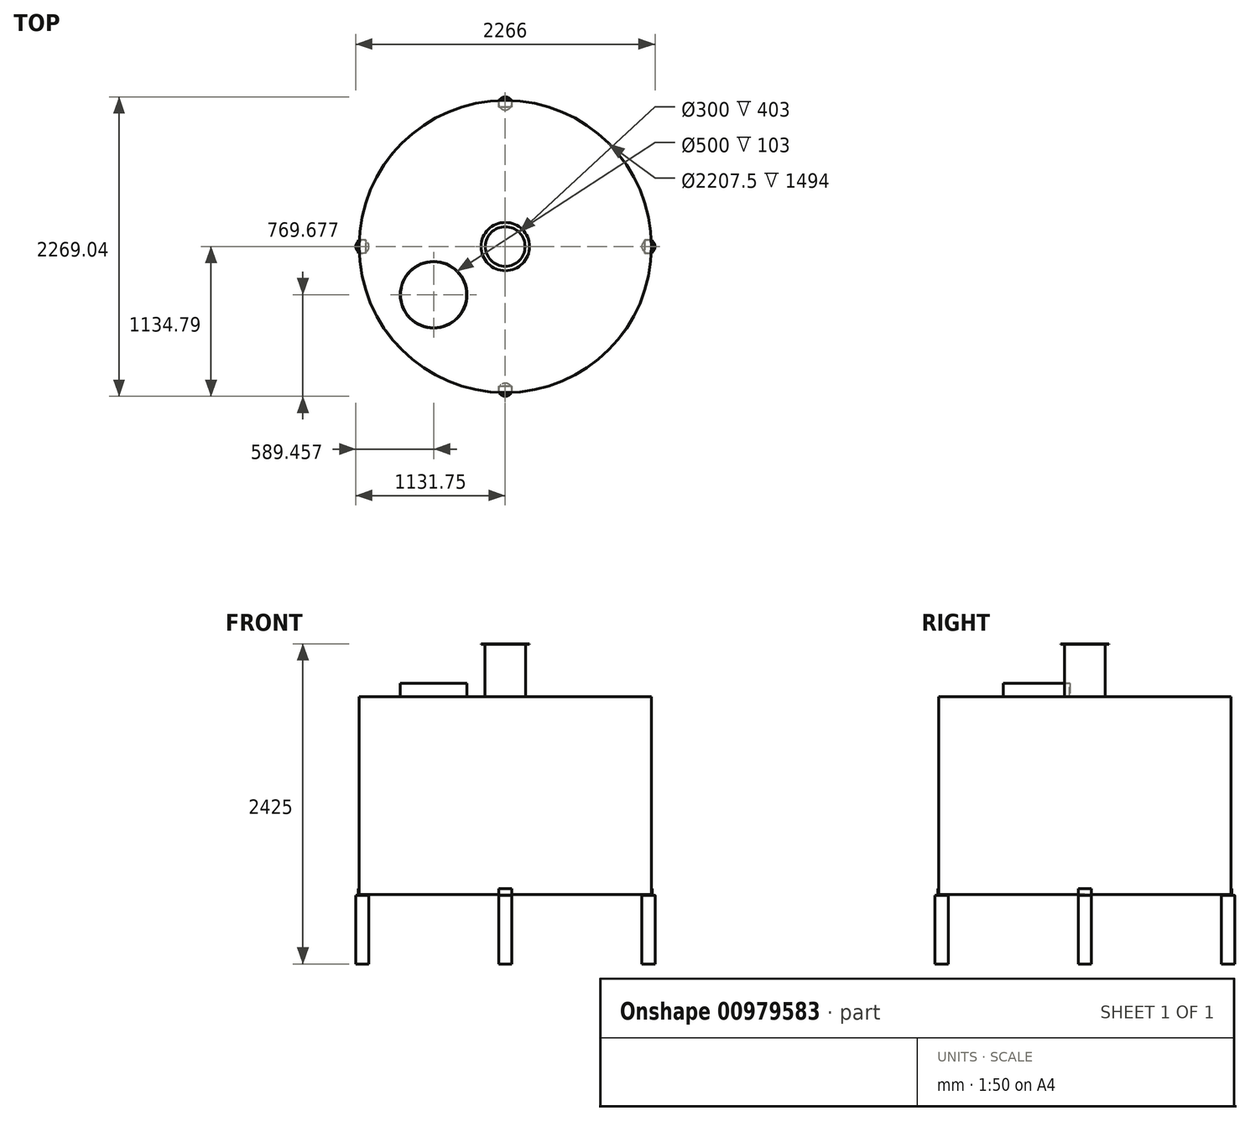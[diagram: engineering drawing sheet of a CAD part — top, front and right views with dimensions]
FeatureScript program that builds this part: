
annotation { "Feature Type Name" : "Feature", "Feature Type Description" : "" }
export const myFeature = defineFeature(function(context is Context, id is Id, definition is map)
    precondition{}
    {
        {
            var Q0;
            Q0=qCreatedBy(makeId("Top.planeOp"),FACE);
            var sketch = newSketch(context, id + "F0", { "sketchPlane" : qUnion([Q0])});
            skCircle(sketch, "E0", {"center": v(0, 0) * mm, "radius": 1106.75 * mm});
            skCircle(sketch, "E1", {"center": v(0, 0) * mm, "radius": 1103.75 * mm});
            skSolve(sketch);
        }
        {
            var Q0;
            Q0=makeQuery(id+"F0.imprint","IMPRINT",FACE,{"disambiguationData":[TD([[makeQuery(id+"F0.imprint","IMPRINT",EDGE,{"derivedFrom":sQuery(id+"F0.wireOp",EDGE,"E0")}),1.0]])]});
            extrude(context, id + "F1", {"entities" : qUnion([Q0]), "oppositeDirection" : true, "depth" : 1500 * mm, "offsetDistance" : 25.4 * mm});
        }
        {
            var Q0;
            Q0=makeQuery(id+"F1.opExtrude","CAP_FACE",FACE,{"disambiguationData":[OSD([sQuery(id+"F0.wireOp",EDGE,"E0"),sQuery(id+"F0.wireOp",EDGE,"E1")])],"isStart":false});
            var sketch = newSketch(context, id + "F2", { "sketchPlane" : qUnion([Q0])});
            skCircle(sketch, "E2", {"center": v(0, 0) * mm, "radius": 1103.75 * mm});
            skSolve(sketch);
        }
        {
            var Q0;
            Q0 = qSketchRegion(id + "F2", true);
            extrude(context, id + "F3", {"entities" : qUnion([Q0]), "operationType" : NewBodyOperationType.ADD, "oppositeDirection" : true, "depth" : 3 * mm, "offsetDistance" : 25.4 * mm});
        }
        {
            var Q0;
            Q0=makeQuery(id+"F1.opExtrude","CAP_FACE",FACE,{"disambiguationData":[OSD([sQuery(id+"F0.wireOp",EDGE,"E0"),sQuery(id+"F0.wireOp",EDGE,"E1")])],"isStart":true});
            var sketch = newSketch(context, id + "F4", { "sketchPlane" : qUnion([Q0])});
            skCircle(sketch, "E3", {"center": v(0, 0) * mm, "radius": 1103.75 * mm});
            skCircle(sketch, "E4", {"center": v(-542.3, -365.11) * mm, "radius": 250 * mm});
            skCircle(sketch, "E5", {"center": v(0, 0) * mm, "radius": 150 * mm});
            skSolve(sketch);
        }
        {
            var Q0;
            Q0 = qSketchRegion(id + "F4", true);
            extrude(context, id + "F5", {"entities" : qUnion([Q0]), "operationType" : NewBodyOperationType.ADD, "oppositeDirection" : true, "depth" : 3 * mm, "offsetDistance" : 25.4 * mm});
        }
        {
            var Q0;
            Q0=makeQuery(id+"F5.boolean.opBoolean","MERGE",FACE,{"derivedFrom":[makeQuery(id+"F1.opExtrude","CAP_FACE",FACE,{"disambiguationData":[OSD([sQuery(id+"F0.wireOp",EDGE,"E0"),sQuery(id+"F0.wireOp",EDGE,"E1")])],"isStart":true}),makeQuery(id+"F5.opExtrude","CAP_FACE",FACE,{"disambiguationData":[OSD([sQuery(id+"F4.wireOp",EDGE,"E3"),sQuery(id+"F4.wireOp",EDGE,"E4"),sQuery(id+"F4.wireOp",EDGE,"E5")])],"isStart":true})]});
            var sketch = newSketch(context, id + "F6", { "sketchPlane" : qUnion([Q0])});
            skCircle(sketch, "E6", {"center": v(-542.3, -365.11) * mm, "radius": 253 * mm});
            skCircle(sketch, "E7", {"center": v(-542.3, -365.11) * mm, "radius": 250 * mm});
            skSolve(sketch);
        }
        {
            var Q0;
            Q0 = qSketchRegion(id + "F6", true);
            extrude(context, id + "F7", {"entities" : qUnion([Q0]), "operationType" : NewBodyOperationType.ADD, "depth" : 100 * mm, "offsetDistance" : 25.4 * mm});
        }
        {
            var Q0;
            Q0=makeQuery(id+"F5.boolean.opBoolean","MERGE",FACE,{"derivedFrom":[makeQuery(id+"F1.opExtrude","CAP_FACE",FACE,{"disambiguationData":[OSD([sQuery(id+"F0.wireOp",EDGE,"E0"),sQuery(id+"F0.wireOp",EDGE,"E1")])],"isStart":true}),makeQuery(id+"F5.opExtrude","CAP_FACE",FACE,{"disambiguationData":[OSD([sQuery(id+"F4.wireOp",EDGE,"E3"),sQuery(id+"F4.wireOp",EDGE,"E4"),sQuery(id+"F4.wireOp",EDGE,"E5")])],"isStart":true})]});
            var sketch = newSketch(context, id + "F8", { "sketchPlane" : qUnion([Q0])});
            skCircle(sketch, "E8", {"center": v(0, 0) * mm, "radius": 153 * mm});
            skCircle(sketch, "E9", {"center": v(0, 0) * mm, "radius": 150 * mm});
            skSolve(sketch);
        }
        {
            var Q0;
            Q0 = qSketchRegion(id + "F8", true);
            extrude(context, id + "F9", {"entities" : qUnion([Q0]), "operationType" : NewBodyOperationType.ADD, "depth" : 400 * mm, "offsetDistance" : 25.4 * mm});
        }
        {
            var Q0;
            Q0=makeQuery(id+"F9.opExtrude","CAP_FACE",FACE,{"disambiguationData":[OSD([sQuery(id+"F8.wireOp",EDGE,"E8"),sQuery(id+"F8.wireOp",EDGE,"E9")])],"isStart":false});
            var sketch = newSketch(context, id + "F10", { "sketchPlane" : qUnion([Q0])});
            skCircle(sketch, "E10", {"center": v(0, 0) * mm, "radius": 183 * mm});
            skCircle(sketch, "E11", {"center": v(0, 0) * mm, "radius": 150 * mm});
            skSolve(sketch);
        }
        {
            var Q0;
            Q0 = qSketchRegion(id + "F10", true);
            extrude(context, id + "F11", {"entities" : qUnion([Q0]), "operationType" : NewBodyOperationType.ADD, "oppositeDirection" : true, "depth" : 3 * mm, "offsetDistance" : 25.4 * mm});
        }
        {
            var Q0;
            Q0=qCreatedBy(makeId("Front.planeOp"),FACE);
            cPlane(context, id + "F12", {"entities" : qUnion([Q0]), "cplaneType" : CPlaneType.OFFSET, "offset" : 1107.3 * mm, "width" : 152.4 * mm, "height" : 152.4 * mm});
        }
        {
            var Q0;
            Q0=qCreatedBy(id+"F12.planeOp",FACE);
            var sketch = newSketch(context, id + "F13", { "sketchPlane" : qUnion([Q0])});
            skLineSegment(sketch, "E12.bottom", {"start": v(-50, -1455) * mm, "end": v(50, -1455) * mm});
            skLineSegment(sketch, "E12.top", {"start": v(-50, -1505) * mm, "end": v(50, -1505) * mm});
            skLineSegment(sketch, "E12.left", {"start": v(-50, -1455) * mm, "end": v(-50, -1505) * mm});
            skLineSegment(sketch, "E12.right", {"start": v(50, -1455) * mm, "end": v(50, -1505) * mm});
            skLineSegment(sketch, "E13", {"start": v(0, -595.76) * mm, "end": v(0, -412.86) * mm, "construction": true});
            skSolve(sketch);
        }
        {
            var Q0;
            Q0 = qSketchRegion(id + "F13", true);
            extrude(context, id + "F14", {"entities" : qUnion([Q0]), "depth" : 5 * mm, "offsetDistance" : 25.4 * mm});
        }
        {
            var Q0;
            Q0=makeQuery(id+"F14.opExtrude","CAP_FACE",FACE,{"disambiguationData":[OSD([sQuery(id+"F13.wireOp",EDGE,"E12.bottom"),sQuery(id+"F13.wireOp",EDGE,"E12.top"),sQuery(id+"F13.wireOp",EDGE,"E12.left"),sQuery(id+"F13.wireOp",EDGE,"E12.right")])],"isStart":true});
            var sketch = newSketch(context, id + "F15", { "sketchPlane" : qUnion([Q0])});
            skLineSegment(sketch, "E14.bottom", {"start": v(-50, -1505) * mm, "end": v(50, -1505) * mm});
            skLineSegment(sketch, "E14.top", {"start": v(-50, -1500) * mm, "end": v(50, -1500) * mm});
            skLineSegment(sketch, "E14.left", {"start": v(-50, -1505) * mm, "end": v(-50, -1500) * mm});
            skLineSegment(sketch, "E14.right", {"start": v(50, -1505) * mm, "end": v(50, -1500) * mm});
            skSolve(sketch);
        }
        {
            var Q0;
            Q0 = qSketchRegion(id + "F15", true);
            extrude(context, id + "F16", {"entities" : qUnion([Q0]), "operationType" : NewBodyOperationType.ADD, "depth" : 50 * mm, "offsetDistance" : 25.4 * mm});
        }
        {
            var Q0;
            Q0=qCreatedBy(id+"F12.planeOp",FACE);
            cPlane(context, id + "F17", {"entities" : qUnion([Q0]), "cplaneType" : CPlaneType.OFFSET, "offset" : 2214.04 * mm, "oppositeDirection" : true, "width" : 152.4 * mm, "height" : 152.4 * mm});
        }
        {
            var Q0;
            Q0=qCreatedBy(id+"F17.planeOp",FACE);
            var sketch = newSketch(context, id + "F18", { "sketchPlane" : qUnion([Q0])});
            skLineSegment(sketch, "E15", {"start": v(0, -83.28) * mm, "end": v(0, -49.38) * mm, "construction": true});
            skLineSegment(sketch, "E16.bottom", {"start": v(50, -1455) * mm, "end": v(-50, -1455) * mm});
            skLineSegment(sketch, "E16.top", {"start": v(50, -1505) * mm, "end": v(-50, -1505) * mm});
            skLineSegment(sketch, "E16.left", {"start": v(50, -1455) * mm, "end": v(50, -1505) * mm});
            skLineSegment(sketch, "E16.right", {"start": v(-50, -1455) * mm, "end": v(-50, -1505) * mm});
            skSolve(sketch);
        }
        {
            var Q0;
            Q0 = qSketchRegion(id + "F18", true);
            extrude(context, id + "F19", {"entities" : qUnion([Q0]), "oppositeDirection" : true, "depth" : 5 * mm, "offsetDistance" : 25.4 * mm});
        }
        {
            var Q0;
            Q0=makeQuery(id+"F19.opExtrude","CAP_FACE",FACE,{"disambiguationData":[OSD([sQuery(id+"F18.wireOp",EDGE,"E16.bottom"),sQuery(id+"F18.wireOp",EDGE,"E16.top"),sQuery(id+"F18.wireOp",EDGE,"E16.left"),sQuery(id+"F18.wireOp",EDGE,"E16.right")])],"isStart":true});
            var sketch = newSketch(context, id + "F20", { "sketchPlane" : qUnion([Q0])});
            skLineSegment(sketch, "E17.bottom", {"start": v(-50, -1505) * mm, "end": v(50, -1505) * mm});
            skLineSegment(sketch, "E17.top", {"start": v(-50, -1500) * mm, "end": v(50, -1500) * mm});
            skLineSegment(sketch, "E17.left", {"start": v(-50, -1505) * mm, "end": v(-50, -1500) * mm});
            skLineSegment(sketch, "E17.right", {"start": v(50, -1505) * mm, "end": v(50, -1500) * mm});
            skSolve(sketch);
        }
        {
            var Q0;
            Q0 = qSketchRegion(id + "F20", true);
            extrude(context, id + "F21", {"entities" : qUnion([Q0]), "operationType" : NewBodyOperationType.ADD, "depth" : 50 * mm, "offsetDistance" : 25.4 * mm});
        }
        {
            var Q0;
            Q0=qCreatedBy(makeId("Right.planeOp"),FACE);
            cPlane(context, id + "F22", {"entities" : qUnion([Q0]), "cplaneType" : CPlaneType.OFFSET, "offset" : 1106.75 * mm, "width" : 152.4 * mm, "height" : 152.4 * mm});
        }
        {
            var Q0;
            Q0=qCreatedBy(id+"F22.planeOp",FACE);
            var sketch = newSketch(context, id + "F23", { "sketchPlane" : qUnion([Q0])});
            skLineSegment(sketch, "E18", {"start": v(0, -73.35) * mm, "end": v(0, -59.65) * mm, "construction": true});
            skLineSegment(sketch, "E19.bottom", {"start": v(-50, -1455) * mm, "end": v(50, -1455) * mm});
            skLineSegment(sketch, "E19.top", {"start": v(-50, -1505) * mm, "end": v(50, -1505) * mm});
            skLineSegment(sketch, "E19.left", {"start": v(-50, -1455) * mm, "end": v(-50, -1505) * mm});
            skLineSegment(sketch, "E19.right", {"start": v(50, -1455) * mm, "end": v(50, -1505) * mm});
            skSolve(sketch);
        }
        {
            var Q0;
            Q0 = qSketchRegion(id + "F23", true);
            extrude(context, id + "F24", {"entities" : qUnion([Q0]), "depth" : 5 * mm, "offsetDistance" : 25.4 * mm});
        }
        {
            var Q0;
            Q0=makeQuery(id+"F24.opExtrude","CAP_FACE",FACE,{"disambiguationData":[OSD([sQuery(id+"F23.wireOp",EDGE,"E19.bottom"),sQuery(id+"F23.wireOp",EDGE,"E19.top"),sQuery(id+"F23.wireOp",EDGE,"E19.left"),sQuery(id+"F23.wireOp",EDGE,"E19.right")])],"isStart":true});
            var sketch = newSketch(context, id + "F25", { "sketchPlane" : qUnion([Q0])});
            skLineSegment(sketch, "E20.bottom", {"start": v(-50, -1505) * mm, "end": v(50, -1505) * mm});
            skLineSegment(sketch, "E20.top", {"start": v(-50, -1500) * mm, "end": v(50, -1500) * mm});
            skLineSegment(sketch, "E20.left", {"start": v(-50, -1505) * mm, "end": v(-50, -1500) * mm});
            skLineSegment(sketch, "E20.right", {"start": v(50, -1505) * mm, "end": v(50, -1500) * mm});
            skSolve(sketch);
        }
        {
            var Q0;
            Q0 = qSketchRegion(id + "F25", true);
            extrude(context, id + "F26", {"entities" : qUnion([Q0]), "operationType" : NewBodyOperationType.ADD, "depth" : 50 * mm, "offsetDistance" : 25.4 * mm});
        }
        {
            var Q0;
            Q0=qCreatedBy(id+"F22.planeOp",FACE);
            cPlane(context, id + "F27", {"entities" : qUnion([Q0]), "cplaneType" : CPlaneType.OFFSET, "offset" : 2213.5 * mm, "oppositeDirection" : true, "width" : 152.4 * mm, "height" : 152.4 * mm});
        }
        {
            var Q0;
            Q0=qCreatedBy(id+"F27.planeOp",FACE);
            var sketch = newSketch(context, id + "F28", { "sketchPlane" : qUnion([Q0])});
            skLineSegment(sketch, "E21", {"start": v(0, -175.15) * mm, "end": v(0, -134.6) * mm, "construction": true});
            skLineSegment(sketch, "E22.bottom", {"start": v(50, -1455) * mm, "end": v(-50, -1455) * mm});
            skLineSegment(sketch, "E22.top", {"start": v(50, -1505) * mm, "end": v(-50, -1505) * mm});
            skLineSegment(sketch, "E22.left", {"start": v(50, -1455) * mm, "end": v(50, -1505) * mm});
            skLineSegment(sketch, "E22.right", {"start": v(-50, -1455) * mm, "end": v(-50, -1505) * mm});
            skSolve(sketch);
        }
        {
            var Q0;
            Q0 = qSketchRegion(id + "F28", true);
            extrude(context, id + "F29", {"entities" : qUnion([Q0]), "oppositeDirection" : true, "depth" : 5 * mm, "offsetDistance" : 25.4 * mm});
        }
        {
            var Q0;
            Q0=makeQuery(id+"F29.opExtrude","CAP_FACE",FACE,{"disambiguationData":[OSD([sQuery(id+"F28.wireOp",EDGE,"E22.bottom"),sQuery(id+"F28.wireOp",EDGE,"E22.top"),sQuery(id+"F28.wireOp",EDGE,"E22.left"),sQuery(id+"F28.wireOp",EDGE,"E22.right")])],"isStart":true});
            var sketch = newSketch(context, id + "F30", { "sketchPlane" : qUnion([Q0])});
            skLineSegment(sketch, "E23.bottom", {"start": v(-50, -1505) * mm, "end": v(50, -1505) * mm});
            skLineSegment(sketch, "E23.top", {"start": v(-50, -1500) * mm, "end": v(50, -1500) * mm});
            skLineSegment(sketch, "E23.left", {"start": v(-50, -1505) * mm, "end": v(-50, -1500) * mm});
            skLineSegment(sketch, "E23.right", {"start": v(50, -1505) * mm, "end": v(50, -1500) * mm});
            skSolve(sketch);
        }
        {
            var Q0;
            Q0 = qSketchRegion(id + "F30", true);
            extrude(context, id + "F31", {"entities" : qUnion([Q0]), "depth" : 50 * mm, "offsetDistance" : 25.4 * mm});
        }
        {
            var Q0;
            Q0=makeQuery(id+"F21.boolean.opBoolean","MERGE",FACE,{"derivedFrom":[makeQuery(id+"F19.opExtrude","SWEPT_FACE",FACE,{"disambiguationData":[OSD([sQuery(id+"F18.wireOp",EDGE,"E16.top")])]}),makeQuery(id+"F21.opExtrude","SWEPT_FACE",FACE,{"disambiguationData":[OSD([sQuery(id+"F20.wireOp",EDGE,"E17.bottom")])]})]});
            var sketch = newSketch(context, id + "F32", { "sketchPlane" : qUnion([Q0])});
            skCircle(sketch, "E24", {"center": v(0, -1084.25) * mm, "radius": 50 * mm});
            skLineSegment(sketch, "E25", {"start": v(65.9, -1084.25) * mm, "end": v(-65.9, -1084.25) * mm, "construction": true});
            skPoint(sketch, "E25.startSnap0", {"position": v(50, -1084.25) * mm});
            skSolve(sketch);
        }
        {
            var Q0;
            Q0 = qSketchRegion(id + "F32", true);
            extrude(context, id + "F33", {"entities" : qUnion([Q0]), "operationType" : NewBodyOperationType.ADD, "depth" : 520 * mm, "offsetDistance" : 25.4 * mm});
        }
        {
            var Q0;
            Q0=makeQuery(id+"F26.boolean.opBoolean","MERGE",FACE,{"derivedFrom":[makeQuery(id+"F24.opExtrude","SWEPT_FACE",FACE,{"disambiguationData":[OSD([sQuery(id+"F23.wireOp",EDGE,"E19.top")])]}),makeQuery(id+"F26.opExtrude","SWEPT_FACE",FACE,{"disambiguationData":[OSD([sQuery(id+"F25.wireOp",EDGE,"E20.bottom")])]})]});
            var sketch = newSketch(context, id + "F34", { "sketchPlane" : qUnion([Q0])});
            skLineSegment(sketch, "E26", {"start": v(1084.25, 75.71) * mm, "end": v(1084.25, -100.63) * mm, "construction": true});
            skPoint(sketch, "E26.startSnap0", {"position": v(1084.25, 50) * mm});
            skPoint(sketch, "E26.endSnap0", {"position": v(1084.25, -50) * mm});
            skCircle(sketch, "E27", {"center": v(1084.25, 0) * mm, "radius": 50 * mm});
            skPoint(sketch, "E27.centerSnap0", {"position": v(1056.75, 0) * mm});
            skSolve(sketch);
        }
        {
            var Q0;
            Q0 = qSketchRegion(id + "F34", true);
            extrude(context, id + "F35", {"entities" : qUnion([Q0]), "operationType" : NewBodyOperationType.ADD, "depth" : 520 * mm, "offsetDistance" : 25.4 * mm});
        }
        {
            var Q0;
            Q0=makeQuery(id+"F16.boolean.opBoolean","MERGE",FACE,{"derivedFrom":[makeQuery(id+"F14.opExtrude","SWEPT_FACE",FACE,{"disambiguationData":[OSD([sQuery(id+"F13.wireOp",EDGE,"E12.top")])]}),makeQuery(id+"F16.opExtrude","SWEPT_FACE",FACE,{"disambiguationData":[OSD([sQuery(id+"F15.wireOp",EDGE,"E14.bottom")])]})]});
            var sketch = newSketch(context, id + "F36", { "sketchPlane" : qUnion([Q0])});
            skLineSegment(sketch, "E28", {"start": v(-50, 1084.79) * mm, "end": v(50, 1084.79) * mm, "construction": true});
            skCircle(sketch, "E29", {"center": v(0, 1084.79) * mm, "radius": 50 * mm});
            skSolve(sketch);
        }
        {
            var Q0;
            Q0 = qSketchRegion(id + "F36", true);
            extrude(context, id + "F37", {"entities" : qUnion([Q0]), "operationType" : NewBodyOperationType.ADD, "depth" : 520 * mm, "offsetDistance" : 25.4 * mm});
        }
        {
            var Q0;
            Q0=makeQuery(id+"F31.opExtrude","SWEPT_FACE",FACE,{"disambiguationData":[OSD([sQuery(id+"F30.wireOp",EDGE,"E23.bottom")])]});
            var sketch = newSketch(context, id + "F38", { "sketchPlane" : qUnion([Q0])});
            skLineSegment(sketch, "E30", {"start": v(-1081.75, -50) * mm, "end": v(-1081.75, 50) * mm, "construction": true});
            skCircle(sketch, "E31", {"center": v(-1081.75, 0) * mm, "radius": 50 * mm});
            skSolve(sketch);
        }
        {
            var Q0;
            Q0 = qSketchRegion(id + "F38", true);
            extrude(context, id + "F39", {"entities" : qUnion([Q0]), "operationType" : NewBodyOperationType.ADD, "depth" : 520 * mm, "offsetDistance" : 25.4 * mm});
        }
    });
